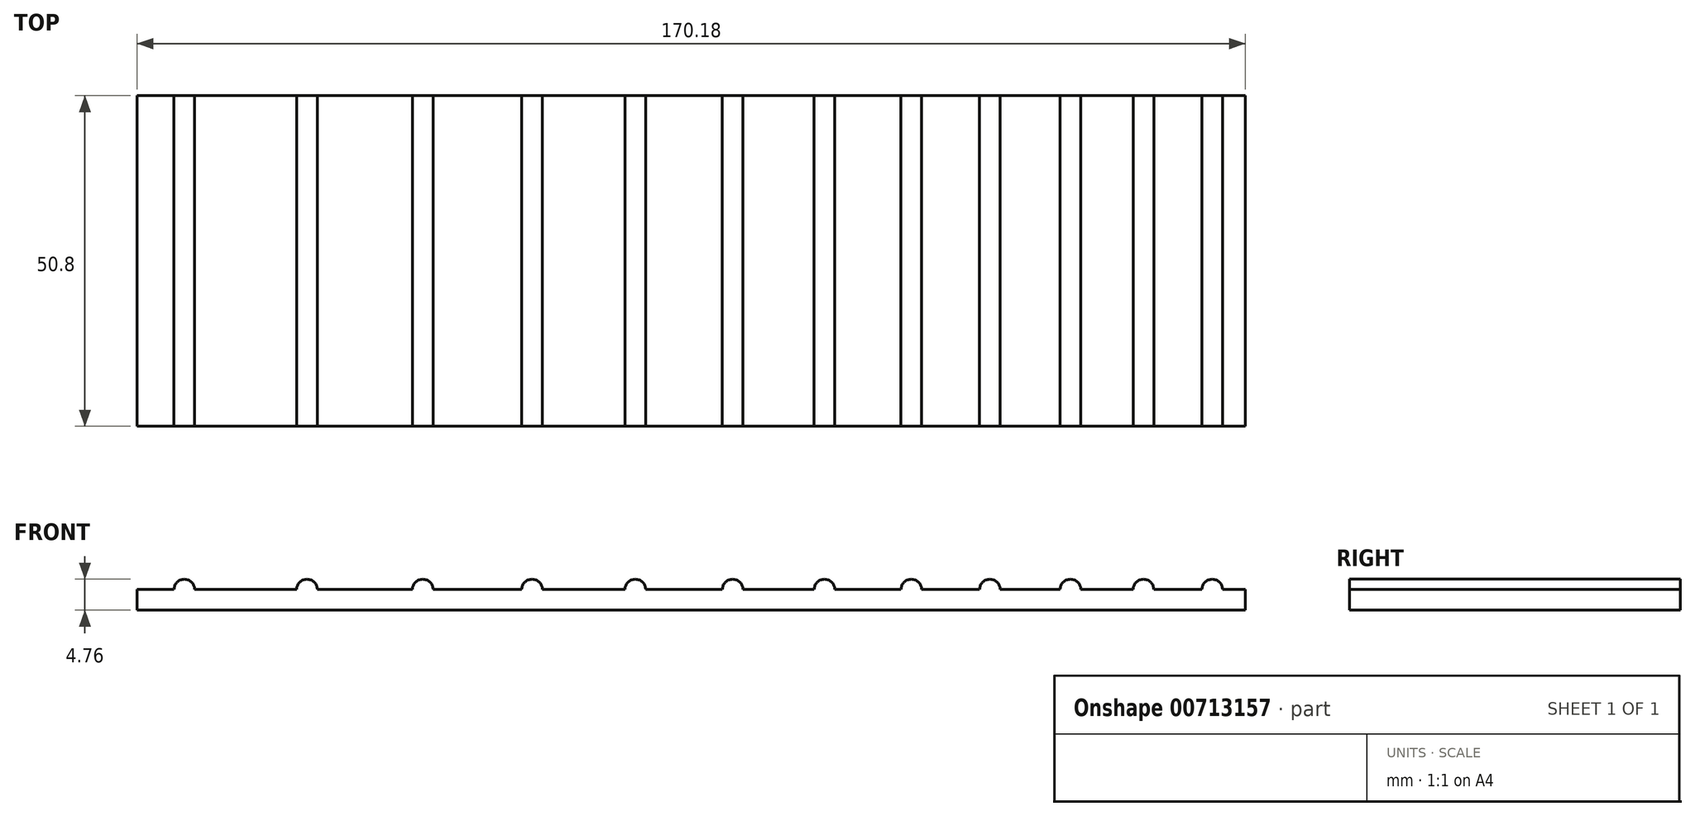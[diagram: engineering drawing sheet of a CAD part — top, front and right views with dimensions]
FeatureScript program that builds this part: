
annotation { "Feature Type Name" : "Feature", "Feature Type Description" : "" }
export const myFeature = defineFeature(function(context is Context, id is Id, definition is map)
    precondition{}
    {
        {
            var Q0;
            Q0=qCreatedBy(makeId("Front.planeOp"),FACE);
            var sketch = newSketch(context, id + "F0", { "sketchPlane" : qUnion([Q0])});
            skLineSegment(sketch, "E0.bottom", {"start": v(12.7, 0) * mm, "end": v(182.88, 0) * mm});
            skLineSegment(sketch, "E0.top", {"start": v(12.7, 3.18) * mm, "end": v(18.38, 3.18) * mm});
            skLineSegment(sketch, "E0.left", {"start": v(12.7, 0) * mm, "end": v(12.7, 3.18) * mm});
            skLineSegment(sketch, "E0.right", {"start": v(182.88, 0) * mm, "end": v(182.88, 3.18) * mm});
            skArc(sketch, "E1", {"start": v(21.55, 3.18) * mm, "mid": v(19.96, 4.76) * mm, "end": v(18.38, 3.18) * mm});
            skArc(sketch, "E2", {"start": v(40.37, 3.18) * mm, "mid": v(38.79, 4.76) * mm, "end": v(37.2, 3.18) * mm});
            skArc(sketch, "E3", {"start": v(58.15, 3.18) * mm, "mid": v(56.57, 4.76) * mm, "end": v(54.98, 3.18) * mm});
            skArc(sketch, "E4", {"start": v(90.8, 3.18) * mm, "mid": v(89.2, 4.76) * mm, "end": v(87.62, 3.18) * mm});
            skArc(sketch, "E5", {"start": v(105.75, 3.18) * mm, "mid": v(104.17, 4.76) * mm, "end": v(102.58, 3.18) * mm});
            skArc(sketch, "E6", {"start": v(119.85, 3.18) * mm, "mid": v(118.26, 4.76) * mm, "end": v(116.67, 3.18) * mm});
            skArc(sketch, "E7", {"start": v(133.18, 3.18) * mm, "mid": v(131.6, 4.76) * mm, "end": v(130, 3.18) * mm});
            skArc(sketch, "E8", {"start": v(145.25, 3.18) * mm, "mid": v(143.66, 4.76) * mm, "end": v(142.07, 3.18) * mm});
            skArc(sketch, "E9", {"start": v(157.62, 3.18) * mm, "mid": v(156.03, 4.76) * mm, "end": v(154.44, 3.18) * mm});
            skArc(sketch, "E10", {"start": v(168.82, 3.18) * mm, "mid": v(167.23, 4.76) * mm, "end": v(165.65, 3.18) * mm});
            skArc(sketch, "E11", {"start": v(179.39, 3.18) * mm, "mid": v(177.8, 4.76) * mm, "end": v(176.21, 3.18) * mm});
            skArc(sketch, "E12", {"start": v(74.94, 3.18) * mm, "mid": v(73.36, 4.76) * mm, "end": v(71.77, 3.18) * mm});
            skLineSegment(sketch, "E13.trimOffspring", {"start": v(21.55, 3.18) * mm, "end": v(37.2, 3.18) * mm});
            skLineSegment(sketch, "E14.trimOffspring", {"start": v(40.37, 3.18) * mm, "end": v(54.98, 3.18) * mm});
            skLineSegment(sketch, "E15.trimOffspring", {"start": v(58.15, 3.18) * mm, "end": v(71.77, 3.18) * mm});
            skLineSegment(sketch, "E16.trimOffspring", {"start": v(74.94, 3.18) * mm, "end": v(87.62, 3.18) * mm});
            skLineSegment(sketch, "E17.trimOffspring", {"start": v(90.8, 3.18) * mm, "end": v(102.58, 3.18) * mm});
            skLineSegment(sketch, "E18.trimOffspring", {"start": v(105.75, 3.18) * mm, "end": v(116.67, 3.18) * mm});
            skLineSegment(sketch, "E19.trimOffspring", {"start": v(119.85, 3.18) * mm, "end": v(130, 3.18) * mm});
            skLineSegment(sketch, "E20.trimOffspring", {"start": v(133.18, 3.18) * mm, "end": v(142.07, 3.18) * mm});
            skLineSegment(sketch, "E21.trimOffspring", {"start": v(145.25, 3.18) * mm, "end": v(154.44, 3.18) * mm});
            skLineSegment(sketch, "E22.trimOffspring", {"start": v(157.62, 3.18) * mm, "end": v(165.65, 3.18) * mm});
            skLineSegment(sketch, "E23.trimOffspring", {"start": v(168.82, 3.18) * mm, "end": v(176.21, 3.18) * mm});
            skLineSegment(sketch, "E24.trimOffspring", {"start": v(179.39, 3.18) * mm, "end": v(182.88, 3.18) * mm});
            skSolve(sketch);
        }
        {
            var Q0;
            Q0=makeQuery(id+"F0.imprint","IMPRINT",FACE,{"disambiguationData":[TD([[makeQuery(id+"F0.imprint","IMPRINT",EDGE,{"derivedFrom":sQuery(id+"F0.wireOp",EDGE,"E0.bottom")}),1.0]])]});
            extrude(context, id + "F1", {"entities" : qUnion([Q0]), "depth" : 50.8 * mm, "offsetDistance" : 25.4 * mm});
        }
    });
